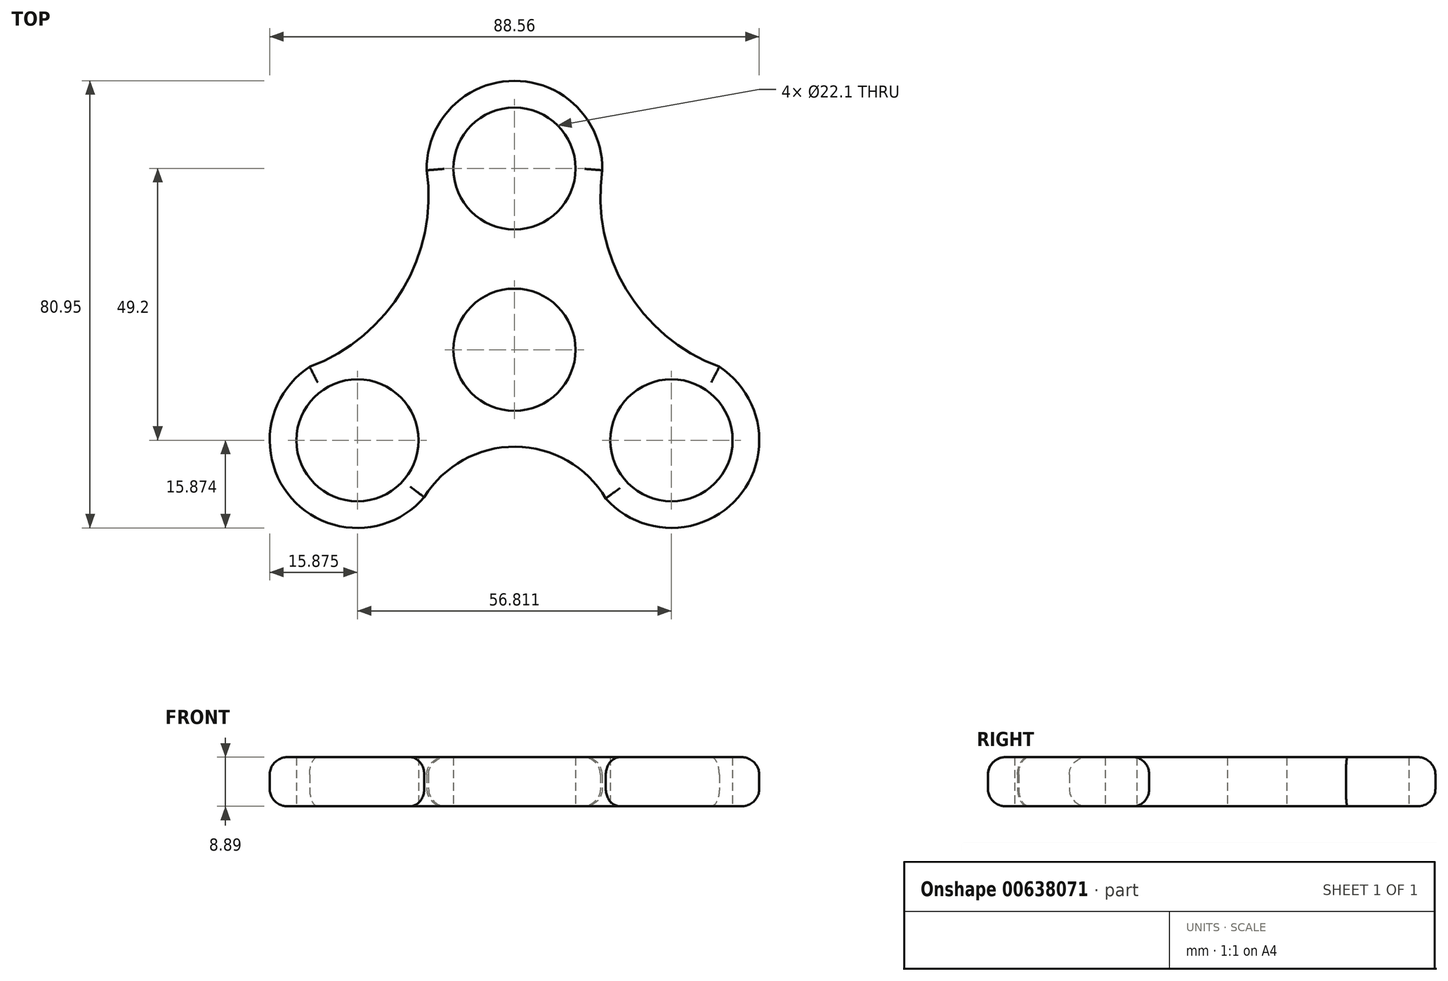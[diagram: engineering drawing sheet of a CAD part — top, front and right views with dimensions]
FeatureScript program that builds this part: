
annotation { "Feature Type Name" : "Feature", "Feature Type Description" : "" }
export const myFeature = defineFeature(function(context is Context, id is Id, definition is map)
    precondition{}
    {
        {
            var Q0;
            Q0=qCreatedBy(makeId("Top.planeOp"),FACE);
            var sketch = newSketch(context, id + "F0", { "sketchPlane" : qUnion([Q0])});
            skCircle(sketch, "E0", {"center": v(0, 59.72) * mm, "radius": 11.05 * mm});
            skCircle(sketch, "E1.1.0", {"center": v(-28.4, 10.52) * mm, "radius": 11.05 * mm});
            skCircle(sketch, "E1.2.0", {"center": v(28.4, 10.52) * mm, "radius": 11.05 * mm});
            skPoint(sketch, "E1.center", {"position": v(0, 26.92) * mm});
            skArc(sketch, "E2", {"start": v(-32.75, 25.8) * mm, "mid": v(-41, 0.85) * mm, "end": v(-14.77, 2.4) * mm});
            skArc(sketch, "E3", {"start": v(15.6, 56.82) * mm, "mid": v(0, 75.6) * mm, "end": v(-15.6, 56.82) * mm});
            skArc(sketch, "E4", {"start": v(14.63, 2.63) * mm, "mid": v(40.9, 0.74) * mm, "end": v(32.75, 25.8) * mm});
            skArc(sketch, "E5", {"start": v(-37.05, 23.84) * mm, "mid": v(-20.19, 37.88) * mm, "end": v(-15.87, 59.41) * mm});
            skArc(sketch, "E6.MirrorCS", {"start": v(37.05, 23.84) * mm, "mid": v(20.19, 37.88) * mm, "end": v(15.87, 59.41) * mm});
            skArc(sketch, "E7", {"start": v(16.52, 0) * mm, "mid": v(0.17, 9.36) * mm, "end": v(-16.32, 0.23) * mm});
            skCircle(sketch, "E8", {"center": v(0, 26.92) * mm, "radius": 11.05 * mm});
            skSolve(sketch);
        }
        {
            var Q0;
            Q0=makeQuery(id+"F0.imprint","IMPRINT",FACE,{"disambiguationData":[TD([[makeQuery(id+"F0.imprint","IMPRINT",EDGE,{"derivedFrom":sQuery(id+"F0.wireOp",EDGE,"E0")}),-1.0]])]});
            extrude(context, id + "F1", {"entities" : qUnion([Q0]), "depth" : 8.9 * mm, "offsetDistance" : 25.4 * mm});
        }
        {
            var Q0;
            Q0=makeQuery(id+"F1.opExtrude","CAP_EDGE",EDGE,{"disambiguationData":[OSD([sQuery(id+"F0.wireOp",EDGE,"E6.MirrorCS")])],"isStart":false});
            var Q1;
            Q1=makeQuery(id+"F1.opExtrude","CAP_EDGE",EDGE,{"disambiguationData":[OSD([sQuery(id+"F0.wireOp",EDGE,"E3")])],"isStart":false});
            var Q2;
            Q2=makeQuery(id+"F1.opExtrude","CAP_EDGE",EDGE,{"disambiguationData":[OSD([sQuery(id+"F0.wireOp",EDGE,"E4")])],"isStart":false});
            var Q3;
            Q3=makeQuery(id+"F1.opExtrude","CAP_EDGE",EDGE,{"disambiguationData":[OSD([sQuery(id+"F0.wireOp",EDGE,"E7")])],"isStart":false});
            var Q4;
            Q4=makeQuery(id+"F1.opExtrude","CAP_EDGE",EDGE,{"disambiguationData":[OSD([sQuery(id+"F0.wireOp",EDGE,"E2")])],"isStart":false});
            var Q5;
            Q5=makeQuery(id+"F1.opExtrude","CAP_EDGE",EDGE,{"disambiguationData":[OSD([sQuery(id+"F0.wireOp",EDGE,"E5")])],"isStart":true});
            var Q6;
            Q6=makeQuery(id+"F1.opExtrude","CAP_EDGE",EDGE,{"disambiguationData":[OSD([sQuery(id+"F0.wireOp",EDGE,"E5")])],"isStart":false});
            var Q7;
            Q7=makeQuery(id+"F1.opExtrude","CAP_EDGE",EDGE,{"disambiguationData":[OSD([sQuery(id+"F0.wireOp",EDGE,"E6.MirrorCS")])],"isStart":true});
            var Q8;
            Q8=makeQuery(id+"F1.opExtrude","CAP_EDGE",EDGE,{"disambiguationData":[OSD([sQuery(id+"F0.wireOp",EDGE,"E4")])],"isStart":true});
            var Q9;
            Q9=makeQuery(id+"F1.opExtrude","CAP_EDGE",EDGE,{"disambiguationData":[OSD([sQuery(id+"F0.wireOp",EDGE,"E3")])],"isStart":true});
            var Q10;
            Q10=makeQuery(id+"F1.opExtrude","CAP_EDGE",EDGE,{"disambiguationData":[OSD([sQuery(id+"F0.wireOp",EDGE,"E2")])],"isStart":true});
            var Q11;
            Q11=makeQuery(id+"F1.opExtrude","CAP_EDGE",EDGE,{"disambiguationData":[OSD([sQuery(id+"F0.wireOp",EDGE,"E7")])],"isStart":true});
            fillet(context, id + "F2", {"entities" : qUnion([Q0, Q1, Q2, Q3, Q4, Q5, Q6, Q7, Q8, Q9, Q10, Q11]), "radius" : 3.17 * mm, "tangentPropagation" : true, "allowEdgeOverflow" : false});
        }
    });
